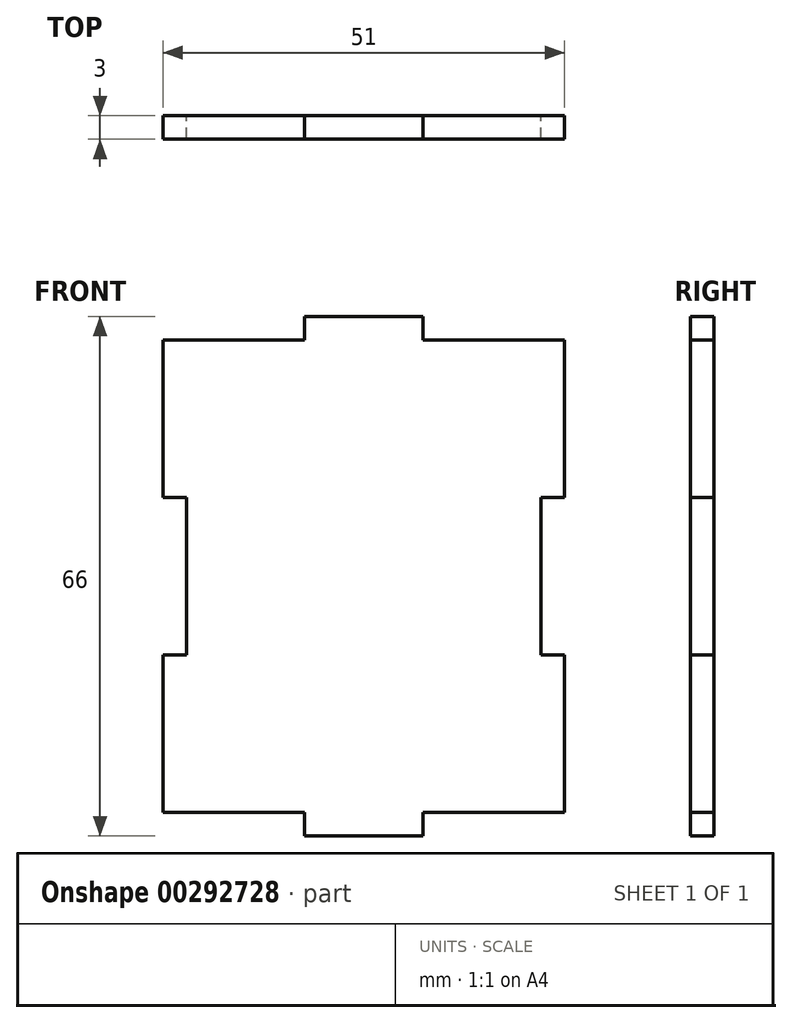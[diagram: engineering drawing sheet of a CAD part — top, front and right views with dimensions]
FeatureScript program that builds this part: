
annotation { "Feature Type Name" : "Feature", "Feature Type Description" : "" }
export const myFeature = defineFeature(function(context is Context, id is Id, definition is map)
    precondition{}
    {
        {
            var Q0;
            Q0=qCreatedBy(makeId("Front.planeOp"),FACE);
            var sketch = newSketch(context, id + "F0", { "sketchPlane" : qUnion([Q0])});
            skLineSegment(sketch, "E0", {"start": v(0, 33) * mm, "end": v(-7.5, 33) * mm});
            skLineSegment(sketch, "E1", {"start": v(-7.5, 33) * mm, "end": v(-7.5, 30) * mm});
            skLineSegment(sketch, "E2", {"start": v(-7.5, 30) * mm, "end": v(-25.5, 30) * mm});
            skLineSegment(sketch, "E3", {"start": v(-25.5, 30) * mm, "end": v(-25.5, 10) * mm});
            skLineSegment(sketch, "E4", {"start": v(-25.5, 10) * mm, "end": v(-22.5, 10) * mm});
            skLineSegment(sketch, "E5", {"start": v(-22.5, 10) * mm, "end": v(-22.5, 0) * mm});
            skLineSegment(sketch, "E6.MirrorCS", {"start": v(25.5, 10) * mm, "end": v(22.5, 10) * mm});
            skLineSegment(sketch, "E7.MirrorCS", {"start": v(7.5, 33) * mm, "end": v(7.5, 30) * mm});
            skLineSegment(sketch, "E8.MirrorCS", {"start": v(22.5, 10) * mm, "end": v(22.5, 0) * mm});
            skLineSegment(sketch, "E9.MirrorCS", {"start": v(0, 33) * mm, "end": v(7.5, 33) * mm});
            skLineSegment(sketch, "E10.MirrorCS", {"start": v(25.5, 30) * mm, "end": v(25.5, 10) * mm});
            skLineSegment(sketch, "E11.MirrorCS", {"start": v(7.5, 30) * mm, "end": v(25.5, 30) * mm});
            skLineSegment(sketch, "E12.MirrorCS", {"start": v(7.5, -33) * mm, "end": v(7.5, -30) * mm});
            skLineSegment(sketch, "E13.MirrorCS", {"start": v(25.5, -10) * mm, "end": v(22.5, -10) * mm});
            skLineSegment(sketch, "E14.MirrorCS", {"start": v(-7.5, -33) * mm, "end": v(-7.5, -30) * mm});
            skLineSegment(sketch, "E15.MirrorCS", {"start": v(-25.5, -10) * mm, "end": v(-22.5, -10) * mm});
            skLineSegment(sketch, "E16.MirrorCS", {"start": v(7.5, -30) * mm, "end": v(25.5, -30) * mm});
            skLineSegment(sketch, "E17.MirrorCS", {"start": v(25.5, -30) * mm, "end": v(25.5, -10) * mm});
            skLineSegment(sketch, "E18.MirrorCS", {"start": v(0, -33) * mm, "end": v(7.5, -33) * mm});
            skLineSegment(sketch, "E19.MirrorCS", {"start": v(22.5, -10) * mm, "end": v(22.5, 0) * mm});
            skLineSegment(sketch, "E20.MirrorCS", {"start": v(-7.5, -30) * mm, "end": v(-25.5, -30) * mm});
            skLineSegment(sketch, "E21.MirrorCS", {"start": v(0, -33) * mm, "end": v(-7.5, -33) * mm});
            skLineSegment(sketch, "E22.MirrorCS", {"start": v(-22.5, -10) * mm, "end": v(-22.5, 0) * mm});
            skLineSegment(sketch, "E23.MirrorCS", {"start": v(-25.5, -30) * mm, "end": v(-25.5, -10) * mm});
            skSolve(sketch);
        }
        {
            var Q0;
            Q0 = qSketchRegion(id + "F0", true);
            extrude(context, id + "F1", {"entities" : qUnion([Q0]), "depth" : 3 * mm});
        }
    });
